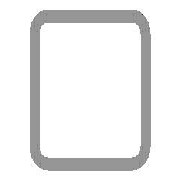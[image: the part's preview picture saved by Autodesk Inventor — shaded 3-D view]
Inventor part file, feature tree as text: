
AUTODESK INVENTOR PART (.ipt)
format: ipt  version: 2022 (Build 260153000, 153)  size: 224,256 bytes
history: native  units: mm (DEFAULTED — no unit token found)
features: other x7, sketch x4, plane x3, split x2, loft x2, sweep x1
ambient origin geometry x8: Origin, YZ Plane, XZ Plane, XY Plane, X Axis, Y Axis, Z Axis, Center Point
bodies: Solid1 (feature_tree), Body (feature_tree)
feature tree (19):
  parser-record x1  (decoder bookkeeping rows leaked as tree rows — omitted from the tree; the rows remain in map.json)
  other  "Driven Length"
  other  "Start Plane"
  other  "End Plane"
  sweep  "Sweep Path"
  other  "Orientation Work Plane"
  plane  "Work Plane5"
  split  "Split1"
  plane  "Work Plane6"
  split  "Split2"
  sketch  "Sketch3"  dims[d7=8.0mm d9=40.0mm]
  plane  "Work Plane3"
  sketch  "Sketch4"  dims[d11=40.0mm d12=4.0mm]
  sketch  "Sketch5"  dims[d13=-0.0mm d14=1675.979797mm]
  other  "Srf1"
  sketch  "Sketch6"  dims[d15=20.0mm d16=20.0mm d17=90.0deg d18=1675.979797mm d19=0.0mm d20=0.0mm d21=8.284271mm d22=0.0mm d23=90.0deg d24=0.0mm d25=90.0deg d26=8.284271mm d27=0.0mm d28=90.0deg d29=0.0mm d30=90.0deg]
  other  "Srf2"
  loft  "LoftSrf1"
  loft  "LoftSrf2"
